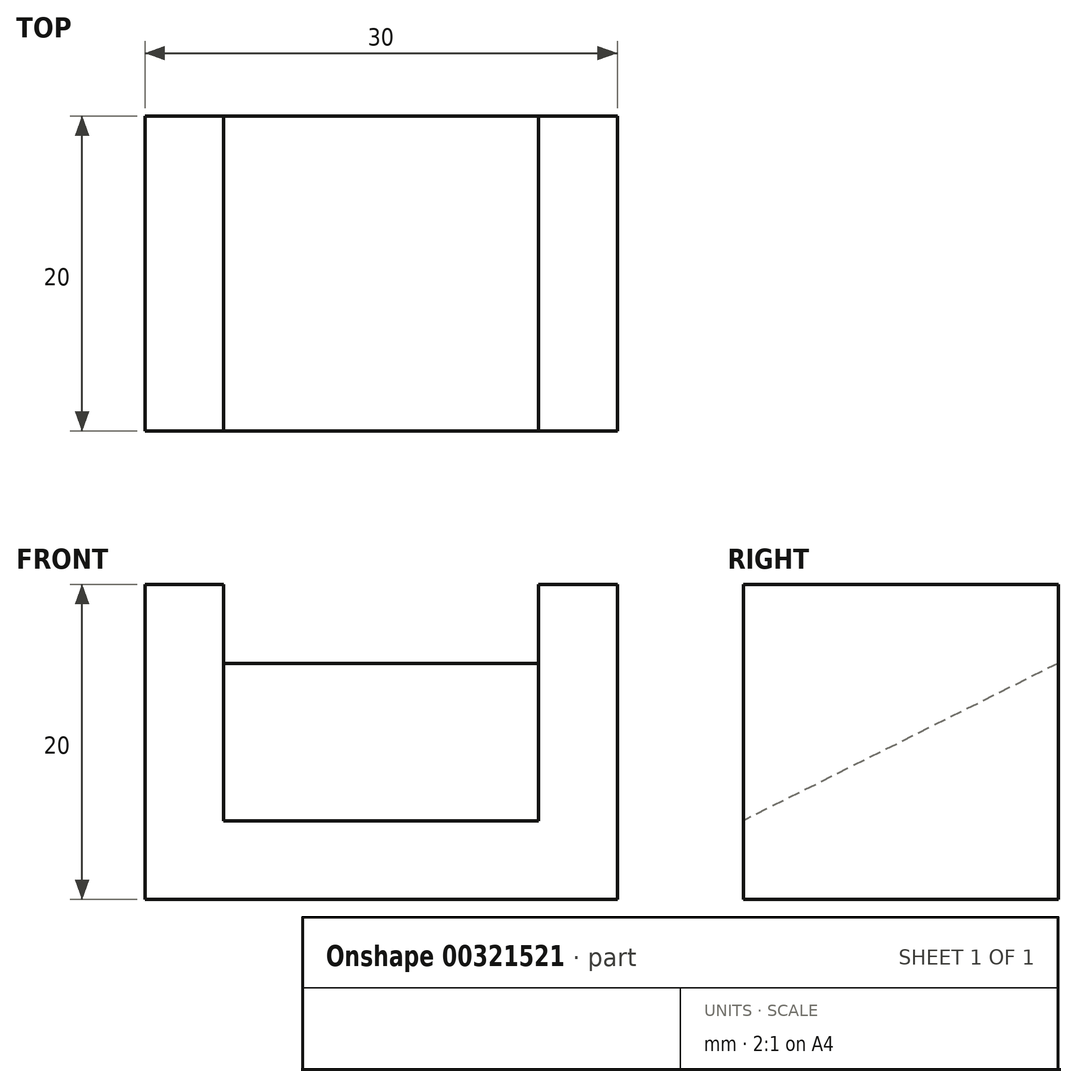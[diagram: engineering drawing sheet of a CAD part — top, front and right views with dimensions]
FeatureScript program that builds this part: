
annotation { "Feature Type Name" : "Feature", "Feature Type Description" : "" }
export const myFeature = defineFeature(function(context is Context, id is Id, definition is map)
    precondition{}
    {
        {
            var Q0;
            Q0=qCreatedBy(makeId("Right.planeOp"),FACE);
            var sketch = newSketch(context, id + "F0", { "sketchPlane" : qUnion([Q0])});
            skLineSegment(sketch, "E0.bottom", {"start": v(0, 0) * mm, "end": v(20, 0) * mm});
            skLineSegment(sketch, "E0.top", {"start": v(0, 20) * mm, "end": v(20, 20) * mm});
            skLineSegment(sketch, "E0.left", {"start": v(0, 0) * mm, "end": v(0, 20) * mm});
            skLineSegment(sketch, "E0.right", {"start": v(20, 0) * mm, "end": v(20, 20) * mm});
            skSolve(sketch);
        }
        {
            var Q0;
            Q0=makeQuery(id+"F0.imprint","IMPRINT",FACE,{"disambiguationData":[TD([[makeQuery(id+"F0.imprint","IMPRINT",EDGE,{"derivedFrom":sQuery(id+"F0.wireOp",EDGE,"E0.bottom")}),1.0]])]});
            extrude(context, id + "F1", {"entities" : qUnion([Q0]), "endBound" : BoundingType.SYMMETRIC, "depth" : 30 * mm});
        }
        {
            var Q0;
            Q0=qCreatedBy(makeId("Right.planeOp"),FACE);
            var sketch = newSketch(context, id + "F2", { "sketchPlane" : qUnion([Q0])});
            skLineSegment(sketch, "E1", {"start": v(0, 5) * mm, "end": v(0, 20) * mm});
            skLineSegment(sketch, "E2", {"start": v(0, 20) * mm, "end": v(20, 20) * mm});
            skLineSegment(sketch, "E3", {"start": v(20, 20) * mm, "end": v(20, 15) * mm});
            skLineSegment(sketch, "E4", {"start": v(20, 15) * mm, "end": v(0, 5) * mm});
            skSolve(sketch);
        }
        {
            var Q0;
            Q0 = qSketchRegion(id + "F2", true);
            extrude(context, id + "F3", {"entities" : qUnion([Q0]), "operationType" : NewBodyOperationType.REMOVE, "endBound" : BoundingType.SYMMETRIC, "depth" : 20 * mm});
        }
    });
